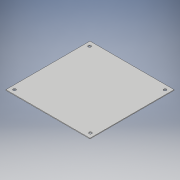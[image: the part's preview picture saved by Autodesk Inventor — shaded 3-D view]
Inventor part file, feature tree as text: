
AUTODESK INVENTOR PART (.ipt)
format: ipt  version: 2018 (Build 220112000, 112)  size: 104,960 bytes
history: native  units: in
note: dims shown in document units (in); Inventor stores cm internally (conversion verified against a paired STEP export)
features: extrude x2, sketch x2
ambient origin geometry x8: Origin, YZ Plane, XZ Plane, XY Plane, X Axis, Y Axis, Z Axis, Center Point
bodies: Solid1 (feature_tree)
feature tree (4):
  extrude  "Extrusion1"  Depth=3.937in
  extrude  "Extrusion2"  Depth=0.031in
  sketch  "Sketch1"  dims[d0=3.937in d1=3.937in]
  sketch  "Sketch2"  dims[d2=0.031in d3=0.0in d4=0.1285in d5=0.1285in d6=0.1285in d7=0.1285in d8=1.0in d9=0.0in]
